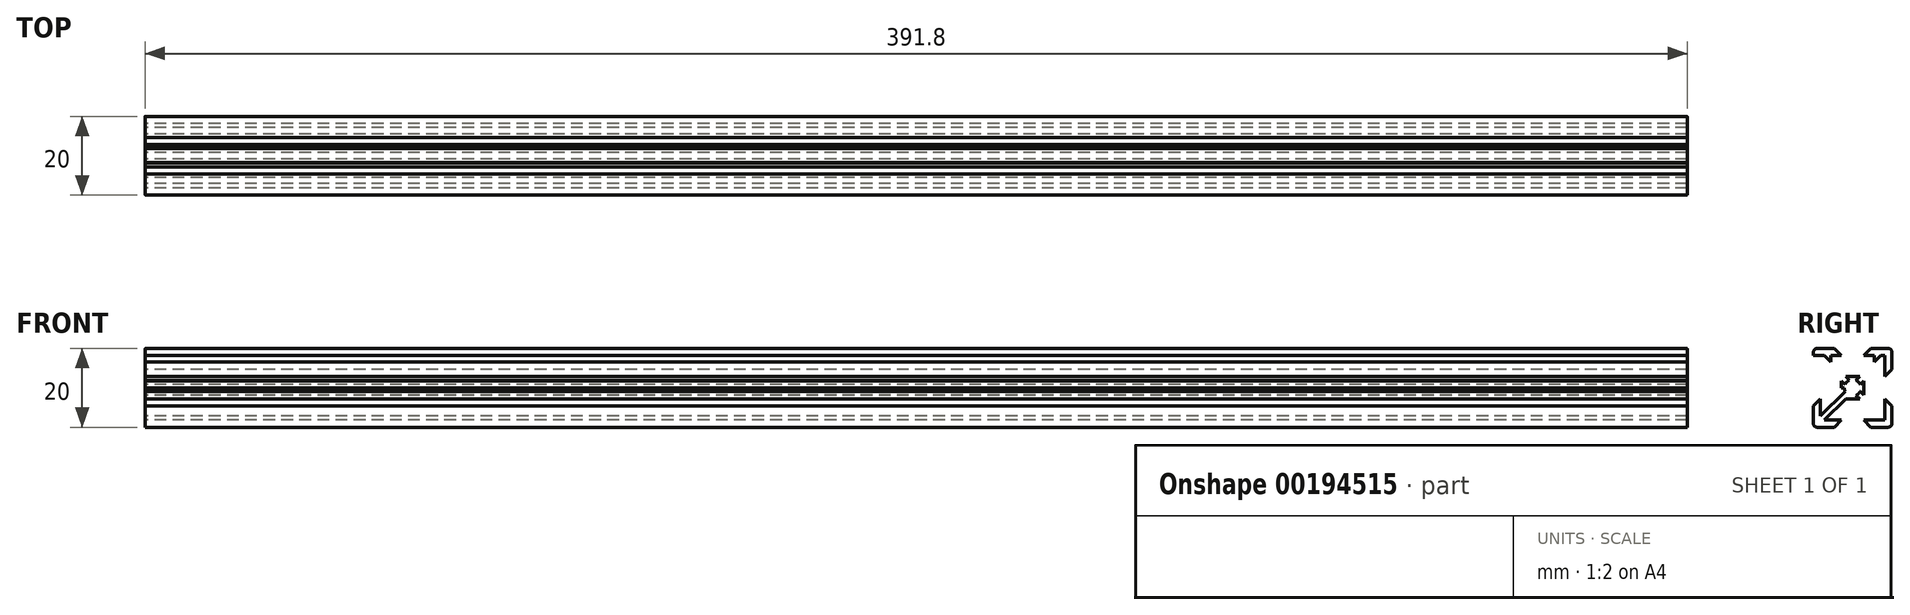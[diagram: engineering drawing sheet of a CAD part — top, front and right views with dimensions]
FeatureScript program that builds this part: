
annotation { "Feature Type Name" : "Feature", "Feature Type Description" : "" }
export const myFeature = defineFeature(function(context is Context, id is Id, definition is map)
    precondition{}
    {
        {
            var Q0;
            Q0=qCreatedBy(makeId("Right.planeOp"),FACE);
            var sketch = newSketch(context, id + "F0", { "sketchPlane" : qUnion([Q0])});
            skArc(sketch, "E0.filletArc", {"start": v(9, -10) * mm, "mid": v(9.7, -9.7) * mm, "end": v(10, -9) * mm});
            skArc(sketch, "E1", {"start": v(2.1, 0) * mm, "mid": v(1.48, -1.48) * mm, "end": v(0, -2.1) * mm});
            skLineSegment(sketch, "E2", {"start": v(0, -2.1) * mm, "end": v(0, -2.84) * mm});
            skLineSegment(sketch, "E3", {"start": v(2.1, 0) * mm, "end": v(2.84, 0) * mm});
            skLineSegment(sketch, "E4", {"start": v(2.84, -8.2) * mm, "end": v(4.64, -10) * mm});
            skLineSegment(sketch, "E5", {"start": v(8.2, -2.84) * mm, "end": v(10, -4.64) * mm});
            skLineSegment(sketch, "E6", {"start": v(4.64, -10) * mm, "end": v(9, -10) * mm});
            skLineSegment(sketch, "E7", {"start": v(10, -4.64) * mm, "end": v(10, -9) * mm});
            skLineSegment(sketch, "E8", {"start": v(2.84, -8.2) * mm, "end": v(10, -8.2) * mm});
            skLineSegment(sketch, "E9", {"start": v(8.2, -2.84) * mm, "end": v(8.2, -10) * mm});
            skLineSegment(sketch, "E10", {"start": v(9, -9) * mm, "end": v(8.2, -8.2) * mm});
            skPoint(sketch, "E11", {"position": v(8.73, -7.67) * mm});
            skPoint(sketch, "E12", {"position": v(7.67, -8.73) * mm});
            skPoint(sketch, "E13", {"position": v(8.2, -8.2) * mm});
            skPoint(sketch, "E14", {"position": v(5.53, -4.47) * mm});
            skPoint(sketch, "E15", {"position": v(4.47, -5.53) * mm});
            skLineSegment(sketch, "E16", {"start": v(7.67, -8.73) * mm, "end": v(4.47, -5.53) * mm});
            skLineSegment(sketch, "E17", {"start": v(8.73, -7.67) * mm, "end": v(5.53, -4.47) * mm});
            skLineSegment(sketch, "E18", {"start": v(5.53, -4.47) * mm, "end": v(1.92, -0.86) * mm});
            skLineSegment(sketch, "E19", {"start": v(4.47, -5.53) * mm, "end": v(0.86, -1.92) * mm});
            skLineSegment(sketch, "E20", {"start": v(8.2, -7.14) * mm, "end": v(8.2, -5.5) * mm});
            skLineSegment(sketch, "E21", {"start": v(7.14, -8.2) * mm, "end": v(5.5, -8.2) * mm});
            skLineSegment(sketch, "E22", {"start": v(5.5, -8.2) * mm, "end": v(5.5, -6.56) * mm});
            skLineSegment(sketch, "E23", {"start": v(8.2, -5.5) * mm, "end": v(6.56, -5.5) * mm});
            skLineSegment(sketch, "E24", {"start": v(2.84, 0) * mm, "end": v(2.84, -1.78) * mm});
            skLineSegment(sketch, "E25", {"start": v(0, -2.84) * mm, "end": v(1.78, -2.84) * mm});
            skArc(sketch, "E26.filletArc", {"start": v(10, 9) * mm, "mid": v(9.7, 9.7) * mm, "end": v(9, 10) * mm});
            skArc(sketch, "E27", {"start": v(0, 2.1) * mm, "mid": v(1.48, 1.48) * mm, "end": v(2.1, 0) * mm});
            skLineSegment(sketch, "E28", {"start": v(0, 2.1) * mm, "end": v(0, 2.84) * mm});
            skLineSegment(sketch, "E29", {"start": v(8.2, 2.84) * mm, "end": v(10, 4.64) * mm});
            skLineSegment(sketch, "E30", {"start": v(2.84, 8.2) * mm, "end": v(4.64, 10) * mm});
            skLineSegment(sketch, "E31", {"start": v(10, 4.64) * mm, "end": v(10, 9) * mm});
            skLineSegment(sketch, "E32", {"start": v(4.64, 10) * mm, "end": v(9, 10) * mm});
            skLineSegment(sketch, "E33", {"start": v(8.2, 2.84) * mm, "end": v(8.2, 10) * mm});
            skLineSegment(sketch, "E34", {"start": v(2.84, 8.2) * mm, "end": v(10, 8.2) * mm});
            skLineSegment(sketch, "E35", {"start": v(9, 9) * mm, "end": v(8.2, 8.2) * mm});
            skPoint(sketch, "E36", {"position": v(7.67, 8.73) * mm});
            skPoint(sketch, "E37", {"position": v(8.73, 7.67) * mm});
            skPoint(sketch, "E38", {"position": v(8.2, 8.2) * mm});
            skPoint(sketch, "E39", {"position": v(4.47, 5.53) * mm});
            skPoint(sketch, "E40", {"position": v(5.53, 4.47) * mm});
            skLineSegment(sketch, "E41", {"start": v(8.73, 7.67) * mm, "end": v(5.53, 4.47) * mm});
            skLineSegment(sketch, "E42", {"start": v(7.67, 8.73) * mm, "end": v(4.47, 5.53) * mm});
            skLineSegment(sketch, "E43", {"start": v(4.47, 5.53) * mm, "end": v(0.86, 1.92) * mm});
            skLineSegment(sketch, "E44", {"start": v(5.53, 4.47) * mm, "end": v(1.92, 0.86) * mm});
            skLineSegment(sketch, "E45", {"start": v(7.14, 8.2) * mm, "end": v(5.5, 8.2) * mm});
            skLineSegment(sketch, "E46", {"start": v(8.2, 7.14) * mm, "end": v(8.2, 5.5) * mm});
            skLineSegment(sketch, "E47", {"start": v(8.2, 5.5) * mm, "end": v(6.56, 5.5) * mm});
            skLineSegment(sketch, "E48", {"start": v(5.5, 8.2) * mm, "end": v(5.5, 6.56) * mm});
            skLineSegment(sketch, "E49", {"start": v(0, 2.84) * mm, "end": v(1.78, 2.84) * mm});
            skLineSegment(sketch, "E50", {"start": v(2.84, 0) * mm, "end": v(2.84, 1.78) * mm});
            skArc(sketch, "E51.filletArc", {"start": v(-9, 10) * mm, "mid": v(-9.7, 9.7) * mm, "end": v(-10, 9) * mm});
            skArc(sketch, "E52", {"start": v(-2.1, 0) * mm, "mid": v(-1.48, 1.48) * mm, "end": v(0, 2.1) * mm});
            skLineSegment(sketch, "E53", {"start": v(-2.1, 0) * mm, "end": v(-2.84, 0) * mm});
            skLineSegment(sketch, "E54", {"start": v(-2.84, 8.2) * mm, "end": v(-4.64, 10) * mm});
            skLineSegment(sketch, "E55", {"start": v(-8.2, 2.84) * mm, "end": v(-10, 4.64) * mm});
            skLineSegment(sketch, "E56", {"start": v(-4.64, 10) * mm, "end": v(-9, 10) * mm});
            skLineSegment(sketch, "E57", {"start": v(-10, 4.64) * mm, "end": v(-10, 9) * mm});
            skLineSegment(sketch, "E58", {"start": v(-2.84, 8.2) * mm, "end": v(-10, 8.2) * mm});
            skLineSegment(sketch, "E59", {"start": v(-8.2, 2.84) * mm, "end": v(-8.2, 10) * mm});
            skLineSegment(sketch, "E60", {"start": v(-9, 9) * mm, "end": v(-8.2, 8.2) * mm});
            skPoint(sketch, "E61", {"position": v(-8.73, 7.67) * mm});
            skPoint(sketch, "E62", {"position": v(-7.67, 8.73) * mm});
            skPoint(sketch, "E63", {"position": v(-8.2, 8.2) * mm});
            skPoint(sketch, "E64", {"position": v(-5.53, 4.47) * mm});
            skPoint(sketch, "E65", {"position": v(-4.47, 5.53) * mm});
            skLineSegment(sketch, "E66", {"start": v(-7.67, 8.73) * mm, "end": v(-4.47, 5.53) * mm});
            skLineSegment(sketch, "E67", {"start": v(-8.73, 7.67) * mm, "end": v(-5.53, 4.47) * mm});
            skLineSegment(sketch, "E68", {"start": v(-5.53, 4.47) * mm, "end": v(-1.92, 0.86) * mm});
            skLineSegment(sketch, "E69", {"start": v(-4.47, 5.53) * mm, "end": v(-0.86, 1.92) * mm});
            skLineSegment(sketch, "E70", {"start": v(-8.2, 7.14) * mm, "end": v(-8.2, 5.5) * mm});
            skLineSegment(sketch, "E71", {"start": v(-7.14, 8.2) * mm, "end": v(-5.5, 8.2) * mm});
            skLineSegment(sketch, "E72", {"start": v(-5.5, 8.2) * mm, "end": v(-5.5, 6.56) * mm});
            skLineSegment(sketch, "E73", {"start": v(-8.2, 5.5) * mm, "end": v(-6.56, 5.5) * mm});
            skLineSegment(sketch, "E74", {"start": v(-2.84, 0) * mm, "end": v(-2.84, 1.78) * mm});
            skLineSegment(sketch, "E75", {"start": v(0, 2.84) * mm, "end": v(-1.78, 2.84) * mm});
            skArc(sketch, "E76.filletArc", {"start": v(-10, -9) * mm, "mid": v(-9.7, -9.7) * mm, "end": v(-9, -10) * mm});
            skArc(sketch, "E77", {"start": v(0, -2.1) * mm, "mid": v(-1.48, -1.48) * mm, "end": v(-2.1, 0) * mm});
            skLineSegment(sketch, "E78", {"start": v(-8.2, -2.84) * mm, "end": v(-10, -4.64) * mm});
            skLineSegment(sketch, "E79", {"start": v(-2.84, -8.2) * mm, "end": v(-4.64, -10) * mm});
            skLineSegment(sketch, "E80", {"start": v(-10, -4.64) * mm, "end": v(-10, -9) * mm});
            skLineSegment(sketch, "E81", {"start": v(-4.64, -10) * mm, "end": v(-9, -10) * mm});
            skLineSegment(sketch, "E82", {"start": v(-8.2, -2.84) * mm, "end": v(-8.2, -10) * mm});
            skLineSegment(sketch, "E83", {"start": v(-2.84, -8.2) * mm, "end": v(-10, -8.2) * mm});
            skLineSegment(sketch, "E84", {"start": v(-9, -9) * mm, "end": v(-8.2, -8.2) * mm});
            skPoint(sketch, "E85", {"position": v(-7.67, -8.73) * mm});
            skPoint(sketch, "E86", {"position": v(-8.73, -7.67) * mm});
            skPoint(sketch, "E87", {"position": v(-8.2, -8.2) * mm});
            skPoint(sketch, "E88", {"position": v(-4.47, -5.53) * mm});
            skPoint(sketch, "E89", {"position": v(-5.53, -4.47) * mm});
            skLineSegment(sketch, "E90", {"start": v(-8.73, -7.67) * mm, "end": v(-5.53, -4.47) * mm});
            skLineSegment(sketch, "E91", {"start": v(-7.67, -8.73) * mm, "end": v(-4.47, -5.53) * mm});
            skLineSegment(sketch, "E92", {"start": v(-4.47, -5.53) * mm, "end": v(-0.86, -1.92) * mm});
            skLineSegment(sketch, "E93", {"start": v(-5.53, -4.47) * mm, "end": v(-1.92, -0.86) * mm});
            skLineSegment(sketch, "E94", {"start": v(-7.14, -8.2) * mm, "end": v(-5.5, -8.2) * mm});
            skLineSegment(sketch, "E95", {"start": v(-8.2, -7.14) * mm, "end": v(-8.2, -5.5) * mm});
            skLineSegment(sketch, "E96", {"start": v(-8.2, -5.5) * mm, "end": v(-6.56, -5.5) * mm});
            skLineSegment(sketch, "E97", {"start": v(-5.5, -8.2) * mm, "end": v(-5.5, -6.56) * mm});
            skLineSegment(sketch, "E98", {"start": v(0, -2.84) * mm, "end": v(-1.78, -2.84) * mm});
            skLineSegment(sketch, "E99", {"start": v(-2.84, 0) * mm, "end": v(-2.84, -1.78) * mm});
            skLineSegment(sketch, "E100", {"start": v(-1.78, -2.84) * mm, "end": v(-2.84, -1.78) * mm});
            skLineSegment(sketch, "E101", {"start": v(-10, 8.2) * mm, "end": v(-10, 9) * mm});
            skLineSegment(sketch, "E102", {"start": v(-9, 10) * mm, "end": v(-4.64, 10) * mm});
            skLineSegment(sketch, "E103", {"start": v(-2.84, 8.2) * mm, "end": v(-7.14, 8.2) * mm});
            skLineSegment(sketch, "E104", {"start": v(-1.78, 2.84) * mm, "end": v(1.78, 2.84) * mm});
            skLineSegment(sketch, "E105", {"start": v(7.14, 8.2) * mm, "end": v(2.84, 8.2) * mm});
            skLineSegment(sketch, "E106", {"start": v(10, 9) * mm, "end": v(10, 4.64) * mm});
            skLineSegment(sketch, "E107", {"start": v(8.2, 2.84) * mm, "end": v(8.2, 5.5) * mm});
            skSolve(sketch);
        }
        {
            var Q0;
            {var subQ5=sQuery(id+"F0.wireOp",EDGE,"E0.filletArc");Q0=makeQuery(id+"F0.imprint","IMPRINT",FACE,{"disambiguationData":[TD([[makeQuery(id+"F0.imprint","IMPRINT",EDGE,{"derivedFrom":subQ5}),1.0]])]});}
            var Q1;
            {var subQ0=sQuery(id+"F0.wireOp",EDGE,"E21");Q1=makeQuery(id+"F0.imprint","IMPRINT",FACE,{"disambiguationData":[TD([[makeQuery(id+"F0.imprint","IMPRINT",EDGE,{"derivedFrom":subQ0}),-1.0]])]});}
            var Q2;
            {var subQ0=sQuery(id+"F0.wireOp",EDGE,"E20");Q2=makeQuery(id+"F0.imprint","IMPRINT",FACE,{"disambiguationData":[TD([[makeQuery(id+"F0.imprint","IMPRINT",EDGE,{"derivedFrom":subQ0}),1.0]])]});}
            var Q3;
            {var subQ6=sQuery(id+"F0.wireOp",EDGE,"E26.filletArc");Q3=makeQuery(id+"F0.imprint","IMPRINT",FACE,{"disambiguationData":[TD([[makeQuery(id+"F0.imprint","IMPRINT",EDGE,{"derivedFrom":subQ6}),1.0]])]});}
            var Q4;
            {var subQ0=sQuery(id+"F0.wireOp",EDGE,"E46");Q4=makeQuery(id+"F0.imprint","IMPRINT",FACE,{"disambiguationData":[TD([[makeQuery(id+"F0.imprint","IMPRINT",EDGE,{"derivedFrom":subQ0}),-1.0]])]});}
            var Q5;
            {var subQ3=sQuery(id+"F0.wireOp",EDGE,"E48");Q5=makeQuery(id+"F0.imprint","IMPRINT",FACE,{"disambiguationData":[TD([[makeQuery(id+"F0.imprint","IMPRINT",EDGE,{"derivedFrom":subQ3}),1.0]])]});}
            var Q6;
            {var subQ6=sQuery(id+"F0.wireOp",EDGE,"E51.filletArc");Q6=makeQuery(id+"F0.imprint","IMPRINT",FACE,{"disambiguationData":[TD([[makeQuery(id+"F0.imprint","IMPRINT",EDGE,{"derivedFrom":subQ6}),1.0]])]});}
            var Q7;
            {var subQ3=sQuery(id+"F0.wireOp",EDGE,"E72");Q7=makeQuery(id+"F0.imprint","IMPRINT",FACE,{"disambiguationData":[TD([[makeQuery(id+"F0.imprint","IMPRINT",EDGE,{"derivedFrom":subQ3}),-1.0]])]});}
            var Q8;
            {var subQ0=sQuery(id+"F0.wireOp",EDGE,"E70");Q8=makeQuery(id+"F0.imprint","IMPRINT",FACE,{"disambiguationData":[TD([[makeQuery(id+"F0.imprint","IMPRINT",EDGE,{"derivedFrom":subQ0}),1.0]])]});}
            var Q9;
            {var subQ5=sQuery(id+"F0.wireOp",EDGE,"E76.filletArc");Q9=makeQuery(id+"F0.imprint","IMPRINT",FACE,{"disambiguationData":[TD([[makeQuery(id+"F0.imprint","IMPRINT",EDGE,{"derivedFrom":subQ5}),1.0]])]});}
            var Q10;
            {var subQ0=sQuery(id+"F0.wireOp",EDGE,"E95");Q10=makeQuery(id+"F0.imprint","IMPRINT",FACE,{"disambiguationData":[TD([[makeQuery(id+"F0.imprint","IMPRINT",EDGE,{"derivedFrom":subQ0}),-1.0]])]});}
            var Q11;
            {var subQ0=sQuery(id+"F0.wireOp",EDGE,"E94");Q11=makeQuery(id+"F0.imprint","IMPRINT",FACE,{"disambiguationData":[TD([[makeQuery(id+"F0.imprint","IMPRINT",EDGE,{"derivedFrom":subQ0}),1.0]])]});}
            var Q12;
            {var subQ4=sQuery(id+"F0.wireOp",EDGE,"E24");Q12=makeQuery(id+"F0.imprint","IMPRINT",FACE,{"disambiguationData":[TD([[makeQuery(id+"F0.imprint","IMPRINT",EDGE,{"derivedFrom":subQ4}),-1.0]])]});}
            var Q13;
            {var subQ4=sQuery(id+"F0.wireOp",EDGE,"E25");Q13=makeQuery(id+"F0.imprint","IMPRINT",FACE,{"disambiguationData":[TD([[makeQuery(id+"F0.imprint","IMPRINT",EDGE,{"derivedFrom":subQ4}),1.0]])]});}
            var Q14;
            {var subQ0=sQuery(id+"F0.wireOp",EDGE,"E2");Q14=makeQuery(id+"F0.imprint","IMPRINT",FACE,{"disambiguationData":[TD([[makeQuery(id+"F0.imprint","IMPRINT",EDGE,{"derivedFrom":subQ0}),1.0]])]});}
            var Q15;
            {var subQ0=sQuery(id+"F0.wireOp",EDGE,"E2");Q15=makeQuery(id+"F0.imprint","IMPRINT",FACE,{"disambiguationData":[TD([[makeQuery(id+"F0.imprint","IMPRINT",EDGE,{"derivedFrom":subQ0}),-1.0]])]});}
            var Q16;
            {var subQ4=sQuery(id+"F0.wireOp",EDGE,"E4");Q16=makeQuery(id+"F0.imprint","IMPRINT",FACE,{"disambiguationData":[TD([[makeQuery(id+"F0.imprint","IMPRINT",EDGE,{"derivedFrom":subQ4}),1.0]])]});}
            var Q17;
            {var subQ1=sQuery(id+"F0.wireOp",EDGE,"E5");Q17=makeQuery(id+"F0.imprint","IMPRINT",FACE,{"disambiguationData":[TD([[makeQuery(id+"F0.imprint","IMPRINT",EDGE,{"derivedFrom":subQ1}),-1.0]])]});}
            var Q18;
            {var subQ0=sQuery(id+"F0.wireOp",EDGE,"E28");Q18=makeQuery(id+"F0.imprint","IMPRINT",FACE,{"disambiguationData":[TD([[makeQuery(id+"F0.imprint","IMPRINT",EDGE,{"derivedFrom":subQ0}),-1.0]])]});}
            var Q19;
            {var subQ0=sQuery(id+"F0.wireOp",EDGE,"E3");Q19=makeQuery(id+"F0.imprint","IMPRINT",FACE,{"disambiguationData":[TD([[makeQuery(id+"F0.imprint","IMPRINT",EDGE,{"derivedFrom":subQ0}),1.0]])]});}
            var Q20;
            {var subQ0=sQuery(id+"F0.wireOp",EDGE,"E28");Q20=makeQuery(id+"F0.imprint","IMPRINT",FACE,{"disambiguationData":[TD([[makeQuery(id+"F0.imprint","IMPRINT",EDGE,{"derivedFrom":subQ0}),1.0]])]});}
            var Q21;
            {var subQ0=sQuery(id+"F0.wireOp",EDGE,"E28");Q21=makeQuery(id+"F0.imprint","IMPRINT",FACE,{"disambiguationData":[TD([[makeQuery(id+"F0.imprint","IMPRINT",EDGE,{"derivedFrom":subQ0}),-1.0]])]});}
            var Q22;
            {var subQ5=sQuery(id+"F0.wireOp",EDGE,"E29");Q22=makeQuery(id+"F0.imprint","IMPRINT",FACE,{"disambiguationData":[TD([[makeQuery(id+"F0.imprint","IMPRINT",EDGE,{"derivedFrom":subQ5}),1.0]])]});}
            var Q23;
            {var subQ4=sQuery(id+"F0.wireOp",EDGE,"E30");Q23=makeQuery(id+"F0.imprint","IMPRINT",FACE,{"disambiguationData":[TD([[makeQuery(id+"F0.imprint","IMPRINT",EDGE,{"derivedFrom":subQ4}),-1.0]])]});}
            var Q24;
            {var subQ4=sQuery(id+"F0.wireOp",EDGE,"E74");Q24=makeQuery(id+"F0.imprint","IMPRINT",FACE,{"disambiguationData":[TD([[makeQuery(id+"F0.imprint","IMPRINT",EDGE,{"derivedFrom":subQ4}),-1.0]])]});}
            var Q25;
            {var subQ1=sQuery(id+"F0.wireOp",EDGE,"E54");Q25=makeQuery(id+"F0.imprint","IMPRINT",FACE,{"disambiguationData":[TD([[makeQuery(id+"F0.imprint","IMPRINT",EDGE,{"derivedFrom":subQ1}),1.0]])]});}
            var Q26;
            {var subQ5=sQuery(id+"F0.wireOp",EDGE,"E57");Q26=makeQuery(id+"F0.imprint","IMPRINT",FACE,{"disambiguationData":[TD([[makeQuery(id+"F0.imprint","IMPRINT",EDGE,{"derivedFrom":subQ5}),-1.0]])]});}
            var Q27;
            {var subQ0=sQuery(id+"F0.wireOp",EDGE,"E53");Q27=makeQuery(id+"F0.imprint","IMPRINT",FACE,{"disambiguationData":[TD([[makeQuery(id+"F0.imprint","IMPRINT",EDGE,{"derivedFrom":subQ0}),1.0]])]});}
            var Q28;
            {var subQ4=sQuery(id+"F0.wireOp",EDGE,"E78");Q28=makeQuery(id+"F0.imprint","IMPRINT",FACE,{"disambiguationData":[TD([[makeQuery(id+"F0.imprint","IMPRINT",EDGE,{"derivedFrom":subQ4}),1.0]])]});}
            var Q29;
            {var subQ1=sQuery(id+"F0.wireOp",EDGE,"E79");Q29=makeQuery(id+"F0.imprint","IMPRINT",FACE,{"disambiguationData":[TD([[makeQuery(id+"F0.imprint","IMPRINT",EDGE,{"derivedFrom":subQ1}),-1.0]])]});}
            var Q30;
            {var subQ5=sQuery(id+"F0.wireOp",EDGE,"E100");Q30=makeQuery(id+"F0.imprint","IMPRINT",FACE,{"disambiguationData":[TD([[makeQuery(id+"F0.imprint","IMPRINT",EDGE,{"derivedFrom":subQ5}),-1.0]])]});}
            var Q31;
            {var subQ6=sQuery(id+"F0.wireOp",EDGE,"E100");Q31=makeQuery(id+"F0.imprint","IMPRINT",FACE,{"disambiguationData":[TD([[makeQuery(id+"F0.imprint","IMPRINT",EDGE,{"derivedFrom":subQ6}),1.0]])]});}
            var Q32;
            {var subQ0=sQuery(id+"F0.wireOp",EDGE,"E18");var subQ15=sQuery(id+"F0.wireOp",EDGE,"E1");var subQ16=makeQuery(id+"F0.imprint","INTERSECT",VERTEX,{"derivedFrom":[subQ15,subQ0]});Q32=makeQuery(id+"F0.imprint","IMPRINT",FACE,{"disambiguationData":[TD([[makeQuery(id+"F0.imprint","IMPRINT",EDGE,{"disambiguationData":[TD([[subQ16,-1.0]])],"derivedFrom":subQ15}),1.0]])]});}
            var Q33;
            {var subQ4=sQuery(id+"F0.wireOp",EDGE,"E43");var subQ5=sQuery(id+"F0.wireOp",EDGE,"E27");var subQ6=makeQuery(id+"F0.imprint","INTERSECT",VERTEX,{"derivedFrom":[subQ5,subQ4]});Q33=makeQuery(id+"F0.imprint","IMPRINT",FACE,{"disambiguationData":[TD([[makeQuery(id+"F0.imprint","IMPRINT",EDGE,{"disambiguationData":[TD([[subQ6,-1.0]])],"derivedFrom":subQ5}),1.0]])]});}
            var Q34;
            {var subQ0=sQuery(id+"F0.wireOp",EDGE,"E68");var subQ9=sQuery(id+"F0.wireOp",EDGE,"E52");var subQ10=makeQuery(id+"F0.imprint","INTERSECT",VERTEX,{"derivedFrom":[subQ9,subQ0]});Q34=makeQuery(id+"F0.imprint","IMPRINT",FACE,{"disambiguationData":[TD([[makeQuery(id+"F0.imprint","IMPRINT",EDGE,{"disambiguationData":[TD([[subQ10,-1.0]])],"derivedFrom":subQ9}),1.0]])]});}
            var Q35;
            Q35=sQuery(id+"F0.wireOp",EDGE,"E1");
            var Q36;
            Q36=sQuery(id+"F0.wireOp",EDGE,"E77");
            var Q37;
            Q37=sQuery(id+"F0.wireOp",EDGE,"E52");
            var Q38;
            Q38=sQuery(id+"F0.wireOp",EDGE,"E27");
            var Q39;
            Q39=sQuery(id+"F0.wireOp",EDGE,"E44");
            var Q40;
            Q40=sQuery(id+"F0.wireOp",EDGE,"E41");
            var Q41;
            Q41=sQuery(id+"F0.wireOp",EDGE,"E47");
            var Q42;
            Q42=sQuery(id+"F0.wireOp",EDGE,"E107");
            var Q43;
            Q43=sQuery(id+"F0.wireOp",EDGE,"E29");
            var Q44;
            Q44=sQuery(id+"F0.wireOp",EDGE,"E106");
            var Q45;
            Q45=sQuery(id+"F0.wireOp",EDGE,"E26.filletArc");
            var Q46;
            Q46=sQuery(id+"F0.wireOp",EDGE,"E32");
            var Q47;
            Q47=sQuery(id+"F0.wireOp",EDGE,"E30");
            var Q48;
            Q48=sQuery(id+"F0.wireOp",EDGE,"E34");
            var Q49;
            Q49=sQuery(id+"F0.wireOp",EDGE,"E48");
            var Q50;
            Q50=sQuery(id+"F0.wireOp",EDGE,"E42");
            var Q51;
            Q51=sQuery(id+"F0.wireOp",EDGE,"E43");
            var Q52;
            Q52=sQuery(id+"F0.wireOp",EDGE,"E104");
            var Q53;
            Q53=sQuery(id+"F0.wireOp",EDGE,"E69");
            var Q54;
            Q54=sQuery(id+"F0.wireOp",EDGE,"E66");
            var Q55;
            Q55=sQuery(id+"F0.wireOp",EDGE,"E72");
            var Q56;
            Q56=sQuery(id+"F0.wireOp",EDGE,"E58");
            var Q57;
            Q57=sQuery(id+"F0.wireOp",EDGE,"E54");
            var Q58;
            Q58=sQuery(id+"F0.wireOp",EDGE,"E56");
            var Q59;
            Q59=sQuery(id+"F0.wireOp",EDGE,"E51.filletArc");
            var Q60;
            Q60=sQuery(id+"F0.wireOp",EDGE,"E57");
            var Q61;
            Q61=sQuery(id+"F0.wireOp",EDGE,"E55");
            extrude(context, id + "F1", {"entities" : qUnion([Q0, Q1, Q2, Q3, Q4, Q5, Q6, Q7, Q8, Q9, Q10, Q11, Q12, Q13, Q14, Q15, Q16, Q17, Q18, Q19, Q20, Q21, Q22, Q23, Q24, Q25, Q26, Q27, Q28, Q29, Q30, Q31, Q32, Q33, Q34]), "surfaceEntities" : qUnion([Q35, Q36, Q37, Q38, Q39, Q40, Q41, Q42, Q43, Q44, Q45, Q46, Q47, Q48, Q49, Q50, Q51, Q52, Q53, Q54, Q55, Q56, Q57, Q58, Q59, Q60, Q61]), "depth" : 431.8 * mm - 40 * mm, "offsetDistance" : 25.4 * mm});
        }
    });
